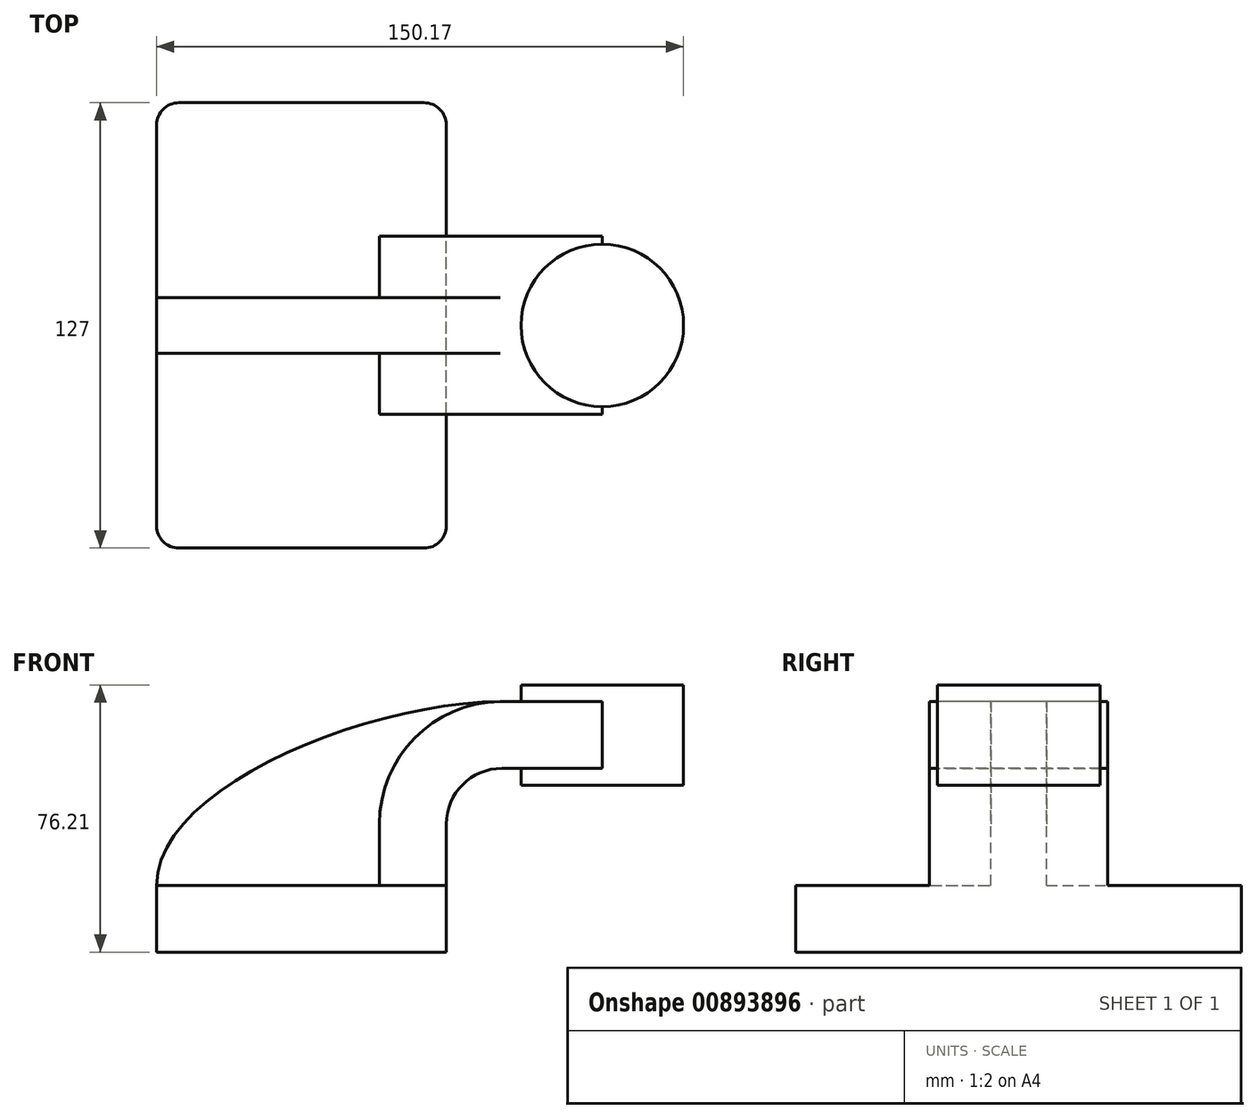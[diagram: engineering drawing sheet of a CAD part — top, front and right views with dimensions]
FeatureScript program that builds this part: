
annotation { "Feature Type Name" : "Feature", "Feature Type Description" : "" }
export const myFeature = defineFeature(function(context is Context, id is Id, definition is map)
    precondition{}
    {
        {
            var Q0;
            Q0=qCreatedBy(makeId("Front.planeOp"),FACE);
            var sketch = newSketch(context, id + "F0", { "sketchPlane" : qUnion([Q0])});
            skLineSegment(sketch, "E0.bottom", {"start": v(41.28, -9.52) * mm, "end": v(-41.28, -9.53) * mm});
            skLineSegment(sketch, "E0.top", {"start": v(41.28, 9.53) * mm, "end": v(-41.28, 9.53) * mm});
            skLineSegment(sketch, "E0.left", {"start": v(41.28, -9.52) * mm, "end": v(41.28, 9.53) * mm});
            skLineSegment(sketch, "E0.right", {"start": v(-41.28, -9.53) * mm, "end": v(-41.28, 9.53) * mm});
            skPoint(sketch, "E0.middle", {"position": v(0, 0) * mm});
            skLineSegment(sketch, "E1.bottom", {"start": v(58.09, 38.1) * mm, "end": v(108.89, 38.1) * mm});
            skLineSegment(sketch, "E1.top", {"start": v(58.09, 66.68) * mm, "end": v(108.89, 66.68) * mm});
            skLineSegment(sketch, "E1.left", {"start": v(58.09, 38.1) * mm, "end": v(58.09, 66.68) * mm});
            skLineSegment(sketch, "E1.right", {"start": v(108.89, 38.1) * mm, "end": v(108.89, 66.68) * mm});
            skPoint(sketch, "E1.middle", {"position": v(83.49, 52.39) * mm});
            skLineSegment(sketch, "E2", {"start": v(41.28, 9.53) * mm, "end": v(41.28, 27) * mm});
            skArc(sketch, "E3", {"start": v(41.27, 27) * mm, "mid": v(45.92, 38.23) * mm, "end": v(57.15, 42.88) * mm});
            skLineSegment(sketch, "E4", {"start": v(57.15, 42.88) * mm, "end": v(85.72, 42.88) * mm});
            skLineSegment(sketch, "E5.0", {"start": v(57.15, 61.93) * mm, "end": v(85.72, 61.93) * mm});
            skArc(sketch, "E5.1", {"start": v(22.23, 27) * mm, "mid": v(32.45, 51.7) * mm, "end": v(57.15, 61.93) * mm});
            skLineSegment(sketch, "E5.2", {"start": v(22.22, 9.53) * mm, "end": v(22.22, 27) * mm});
            skLineSegment(sketch, "E6", {"start": v(85.72, 38.1) * mm, "end": v(85.72, 66.68) * mm});
            skFitSpline(sketch, "E7", {"points": [v(-41.28, 9.52) * mm, v(57.15, 61.93) * mm], "startDerivative": vector(0.23, 84.17) * mm, "endDerivative": vector(116.33, 0.5) * mm});
            skSolve(sketch);
        }
        {
            var Q0;
            Q0=makeQuery(id+"F0.imprint","IMPRINT",FACE,{"disambiguationData":[TD([[makeQuery(id+"F0.imprint","IMPRINT",EDGE,{"derivedFrom":sQuery(id+"F0.wireOp",EDGE,"E0.bottom")}),-1.0]])]});
            extrude(context, id + "F1", {"entities" : qUnion([Q0]), "endBound" : BoundingType.SYMMETRIC, "depth" : 127 * mm, "offsetDistance" : 25.4 * mm});
        }
        {
            var Q0;
            {var subQ1=sQuery(id+"F0.wireOp",EDGE,"E2");Q0=makeQuery(id+"F0.imprint","IMPRINT",FACE,{"disambiguationData":[TD([[makeQuery(id+"F0.imprint","IMPRINT",EDGE,{"derivedFrom":subQ1}),1.0]])]});}
            var Q1;
            {var subQ0=sQuery(id+"F0.wireOp",EDGE,"E4");var subQ1=sQuery(id+"F0.wireOp",EDGE,"E1.left");var subQ2=makeQuery(id+"F0.imprint","INTERSECT",VERTEX,{"derivedFrom":[subQ1,subQ0]});Q1=makeQuery(id+"F0.imprint","IMPRINT",FACE,{"disambiguationData":[TD([[makeQuery(id+"F0.imprint","IMPRINT",EDGE,{"disambiguationData":[TD([[subQ2,-1.0]])],"derivedFrom":subQ1}),-1.0]])]});}
            extrude(context, id + "F2", {"entities" : qUnion([Q0, Q1]), "operationType" : NewBodyOperationType.ADD, "endBound" : BoundingType.SYMMETRIC, "depth" : 50.8 * mm, "offsetDistance" : 25.4 * mm});
        }
        {
            var Q0;
            {var subQ3=sQuery(id+"F0.wireOp",EDGE,"E5.2");Q0=makeQuery(id+"F0.imprint","IMPRINT",FACE,{"disambiguationData":[TD([[makeQuery(id+"F0.imprint","IMPRINT",EDGE,{"derivedFrom":subQ3}),1.0]])]});}
            extrude(context, id + "F3", {"entities" : qUnion([Q0]), "operationType" : NewBodyOperationType.ADD, "endBound" : BoundingType.SYMMETRIC, "depth" : 15.88 * mm, "offsetDistance" : 25.4 * mm});
        }
        {
            var Q0;
            {var subQ4=sQuery(id+"F0.wireOp",EDGE,"E1.right");Q0=makeQuery(id+"F0.imprint","IMPRINT",FACE,{"disambiguationData":[TD([[makeQuery(id+"F0.imprint","IMPRINT",EDGE,{"derivedFrom":subQ4}),1.0]])]});}
            var Q1;
            Q1=sQuery(id+"F0.wireOp",EDGE,"E6");
            revolve(context, id + "F4", {"operationType" : NewBodyOperationType.ADD, "surfaceOperationType" : NewSurfaceOperationType.NEW, "entities" : qUnion([Q0]), "axis" : qUnion([Q1]), "revolveType" : RevolveType.FULL});
        }
        {
            var Q0;
            Q0=makeQuery(id+"F1.opExtrude","CAP_EDGE",EDGE,{"disambiguationData":[OSD([sQuery(id+"F0.wireOp",EDGE,"E0.right")])],"isStart":false});
            var Q1;
            Q1=makeQuery(id+"F1.opExtrude","CAP_EDGE",EDGE,{"disambiguationData":[OSD([sQuery(id+"F0.wireOp",EDGE,"E0.left")])],"isStart":false});
            var Q2;
            Q2=makeQuery(id+"F1.opExtrude","CAP_EDGE",EDGE,{"disambiguationData":[OSD([sQuery(id+"F0.wireOp",EDGE,"E0.left")])],"isStart":true});
            var Q3;
            Q3=makeQuery(id+"F1.opExtrude","CAP_EDGE",EDGE,{"disambiguationData":[OSD([sQuery(id+"F0.wireOp",EDGE,"E0.right")])],"isStart":true});
            fillet(context, id + "F5", {"entities" : qUnion([Q0, Q1, Q2, Q3]), "radius" : 6.35 * mm, "tangentPropagation" : true, "allowEdgeOverflow" : false});
        }
    });
